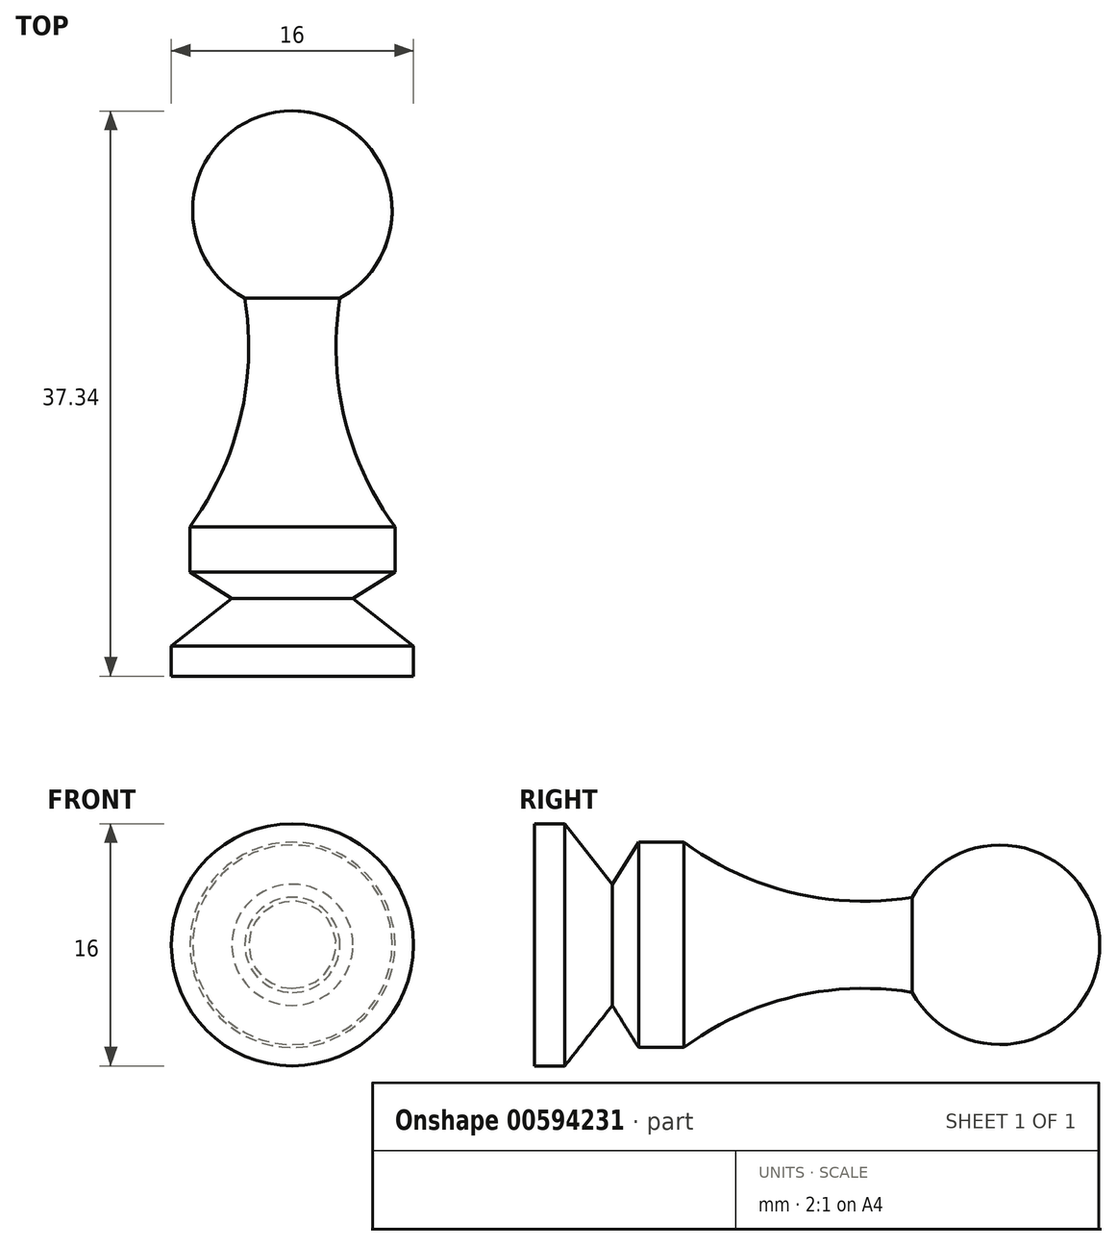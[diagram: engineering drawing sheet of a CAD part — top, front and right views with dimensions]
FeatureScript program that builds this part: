
annotation { "Feature Type Name" : "Feature", "Feature Type Description" : "" }
export const myFeature = defineFeature(function(context is Context, id is Id, definition is map)
    precondition{}
    {
        {
            var Q0;
            Q0=qCreatedBy(makeId("Top.planeOp"),FACE);
            var sketch = newSketch(context, id + "F0", { "sketchPlane" : qUnion([Q0])});
            skLineSegment(sketch, "E0", {"start": v(0, 0) * mm, "end": v(0, 37.34) * mm});
            skArc(sketch, "E1", {"start": v(0, 37.34) * mm, "mid": v(-6.39, 32.38) * mm, "end": v(-3.14, 24.96) * mm});
            skLineSegment(sketch, "E2", {"start": v(0, 0) * mm, "end": v(-8, 0) * mm});
            skLineSegment(sketch, "E3", {"start": v(-8, 0) * mm, "end": v(-8, 2) * mm});
            skLineSegment(sketch, "E4", {"start": v(-8, 2) * mm, "end": v(-4, 5.14) * mm});
            skLineSegment(sketch, "E5", {"start": v(-4, 5.14) * mm, "end": v(-6.78, 6.87) * mm});
            skLineSegment(sketch, "E6", {"start": v(-6.78, 6.87) * mm, "end": v(-6.78, 9.87) * mm});
            skPoint(sketch, "E7.trimOffspring.end.orphan", {"position": v(9.9, 26.07) * mm});
            skArc(sketch, "E8", {"start": v(-6.78, 9.87) * mm, "mid": v(-3.44, 17.05) * mm, "end": v(-3.14, 24.96) * mm});
            skSolve(sketch);
        }
        {
            var Q0;
            Q0=makeQuery(id+"F0.imprint","IMPRINT",FACE,{"disambiguationData":[TD([[makeQuery(id+"F0.imprint","IMPRINT",EDGE,{"derivedFrom":sQuery(id+"F0.wireOp",EDGE,"E0")}),1.0]])]});
            var Q1;
            Q1=sQuery(id+"F0.wireOp",EDGE,"E0");
            revolve(context, id + "F1", {"entities" : qUnion([Q0]), "axis" : qUnion([Q1]), "revolveType" : RevolveType.FULL});
        }
    });
